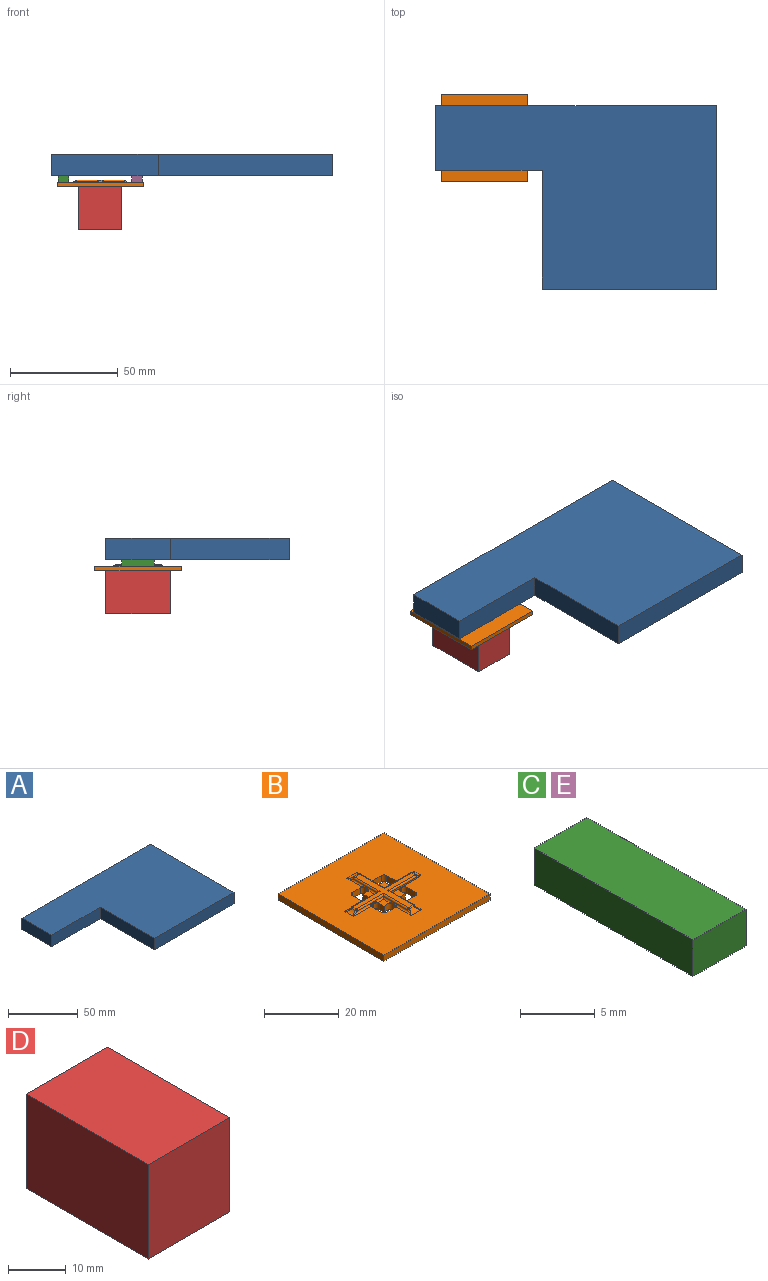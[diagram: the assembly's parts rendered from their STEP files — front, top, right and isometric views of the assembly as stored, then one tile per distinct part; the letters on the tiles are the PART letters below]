
ASSEMBLY  parts=5 mates=4
PART A: 8 faces, bbox 130x84.9x10 mm
  f0: plane 49.29x10mm, normal (0,-1,0), area 492.9mm2, adj f1,f5,f6,f7
  f1: plane 54.94x10mm, normal (-1,0,0), area 549.4mm2, adj f0,f2,f6,f7
  f2: plane 80.71x10mm, normal (0,-1,0), area 807.1mm2, adj f1,f3,f6,f7
  f3: plane 84.94x10mm, normal (1,0,0), area 849.4mm2, adj f2,f4,f6,f7
  f4: plane 130x10mm, normal (0,1,0), area 1300mm2, adj f3,f5,f6,f7
  f5: plane 30x10mm, normal (-1,0,0), area 300mm2, adj f0,f4,f6,f7
  f6: plane 130x84.94mm, normal (0,0,1), area 8334mm2, adj f0,f1,f2,f3,f4,f5
  f7: plane 130x84.94mm, normal (0,0,-1), area 8334mm2, adj f0,f1,f2,f3,f4,f5
PART B: 123 faces, bbox 40.1x40.1x3.1 mm
  f0: plane 40.13x40.13mm, normal (0,0,1), area 1357.2mm2, adj f3,f4,f5,f10,f11,f12,f13,f14
  f1: plane 2.59x2.31mm, normal (0,0,1), area 5.1mm2, adj f7,f8,f39,f40,f76,f79
  f2: plane 2.59x2.31mm, normal (0,0,1), area 5.1mm2, adj f22,f23,f36,f42,f95,f98
  f3: plane 40x2mm, normal (1,0,0), area 80mm2, adj f0,f4,f30,f32
  f4: plane 40x2mm, normal (0,1,0), area 80mm2, adj f0,f3,f5,f32
  f5: plane 40x2mm, normal (-1,0,0), area 80mm2, adj f0,f4,f30,f32
  f6: plane 2x0.5mm, normal (0,1,0), area 1mm2, adj f32,f39,f49,f80
  f7: plane 2x1.79mm, normal (1,0,0), area 3.6mm2, adj f1,f8,f32,f39
  f8: plane 2x1.5mm, normal (0,1,0), area 3mm2, adj f1,f7,f32,f40
  f9: plane 2x0.5mm, normal (1,0,0), area 1mm2, adj f32,f40,f47,f72
  f10: plane 3x2mm, normal (0,-1,0), area 6mm2, adj f0,f32,f47,f48
  f11: plane 2x1.79mm, normal (1,0,0), area 3.6mm2, adj f0,f27,f32,f38
  f12: plane 2x0.5mm, normal (0,-1,0), area 1mm2, adj f0,f32,f38,f50
  f13: plane 3.29x2mm, normal (-1,0,0), area 6.6mm2, adj f0,f32,f50,f51
  f14: plane 4x2.19mm, normal (0,1,0), area 8mm2, adj f0,f15,f32,f51,f86
  f15: plane 2.19x1.5mm, normal (1,0,0), area 3.3mm2, adj f14,f32,f37,f86
  f16: plane 2x1.79mm, normal (-1,0,0), area 3.6mm2, adj f28,f31,f32,f33
  f17: plane 2x0.5mm, normal (0,1,0), area 1mm2, adj f32,f33,f34,f67
  f18: plane 3.29x2mm, normal (1,0,0), area 6.6mm2, adj f0,f32,f34,f45
  f19: plane 3x2mm, normal (0,-1,0), area 6mm2, adj f0,f32,f45,f46
  f20: plane 2x0.5mm, normal (-1,0,0), area 1mm2, adj f32,f41,f46,f61
  f21: plane 2x0.5mm, normal (0,-1,0), area 1mm2, adj f32,f35,f36,f88
  f22: plane 2x1.79mm, normal (-1,0,0), area 3.6mm2, adj f2,f23,f32,f36
  f23: plane 2x1.5mm, normal (0,-1,0), area 3mm2, adj f2,f22,f32,f42
  f24: plane 2x0.5mm, normal (-1,0,0), area 1mm2, adj f32,f42,f43,f94
  f25: plane 3x2mm, normal (0,1,0), area 6mm2, adj f0,f32,f43,f44
  f26: plane 3.29x2mm, normal (-1,0,0), area 6.6mm2, adj f0,f32,f48,f49
  f27: plane 2x1.5mm, normal (0,-1,0), area 3mm2, adj f0,f11,f32,f37
  f28: plane 2x1.5mm, normal (0,1,0), area 3mm2, adj f16,f31,f32,f41
  f29: plane 3.29x2mm, normal (1,0,0), area 6.6mm2, adj f0,f32,f35,f44
  f30: plane 40x2mm, normal (0,-1,0), area 80mm2, adj f0,f3,f5,f32
  f31: plane 2.59x2.31mm, normal (0,0,1), area 5.1mm2, adj f16,f28,f33,f41,f68,f71
  f32: plane 40x40mm, normal (0,0,-1), area 1526.2mm2, adj f3,f4,f5,f6,f7,f8,f9,f10
  f33: cylinder r=1mm len=2mm, axis (0,0,1), area 3.1mm2, adj f16,f17,f31,f32,f70
  f34: cylinder r=1mm len=2mm, axis (0,0,-1), area 3.1mm2, adj f0,f17,f18,f32,f63
  f35: cylinder r=1mm len=2mm, axis (0,0,1), area 3.1mm2, adj f0,f21,f29,f32,f87
  f36: cylinder r=1mm len=2mm, axis (0,0,-1), area 3.1mm2, adj f2,f21,f22,f32,f91
  f37: cylinder r=1mm len=2.19mm, axis (0,0,-1), area 3.2mm2, adj f0,f15,f27,f32,f86
  f38: cylinder r=1mm len=2mm, axis (0,0,1), area 3.1mm2, adj f0,f11,f12,f32
  f39: cylinder r=1mm len=2mm, axis (0,0,-1), area 3.1mm2, adj f1,f6,f7,f32,f77
  f40: cylinder r=1mm len=2mm, axis (0,0,1), area 3.1mm2, adj f1,f8,f9,f32,f74
  f41: cylinder r=1mm len=2mm, axis (0,0,-1), area 3.1mm2, adj f20,f28,f31,f32,f64
  f42: cylinder r=1mm len=2mm, axis (0,0,1), area 3.1mm2, adj f2,f23,f24,f32,f97
  f43: cylinder r=1mm len=2mm, axis (0,0,-1), area 3.1mm2, adj f0,f24,f25,f32,f90
  f44: cylinder r=1mm len=2mm, axis (0,0,-1), area 3.1mm2, adj f0,f25,f29,f32
  f45: cylinder r=1mm len=2mm, axis (0,0,1), area 3.1mm2, adj f0,f18,f19,f32
  f46: cylinder r=1mm len=2mm, axis (0,0,1), area 3.1mm2, adj f0,f19,f20,f32,f60
  f47: cylinder r=1mm len=2mm, axis (0,0,-1), area 3.1mm2, adj f0,f9,f10,f32,f73
  f48: cylinder r=1mm len=2mm, axis (0,0,-1), area 3.1mm2, adj f0,f10,f26,f32
  f49: cylinder r=1mm len=2mm, axis (0,0,1), area 3.1mm2, adj f0,f6,f26,f32,f82
  f50: cylinder r=1mm len=2mm, axis (0,0,-1), area 3.1mm2, adj f0,f12,f13,f32
  f51: cylinder r=1mm len=2mm, axis (0,0,1), area 3.1mm2, adj f0,f13,f14,f32
  f52: plane 2.11x0.2mm, normal (0,-1,0), area 0.3mm2, adj f87,f88,f91,f92
  f53: plane 2.08x0.19mm, normal (-1,0,0), area 0.2mm2, adj f90,f94,f96,f97
  f54: plane 10.25x0.5mm, normal (0,-1,0), area 4.9mm2, adj f0,f84,f86,f113
  f55: plane 2.11x0.2mm, normal (0,1,0), area 0.3mm2, adj f77,f80,f81,f82
  f56: plane 2.09x0.19mm, normal (1,0,0), area 0.2mm2, adj f72,f73,f74,f78
  f57: plane 2.08x0.19mm, normal (-1,0,0), area 0.2mm2, adj f60,f61,f64,f65
  f58: plane 2.11x0.2mm, normal (0,1,0), area 0.3mm2, adj f63,f67,f69,f70
  f59: plane 22.28x20.2mm, normal (0,0,1), area 61.2mm2, adj f65,f69,f78,f81,f84,f85,f92,f96
  f60: bspline ~0.98x0.52mm, area 0.4mm2, adj f46,f57,f61,f62
  f61: cylinder r=0.5mm len=0.5mm, axis (0,-1,0), area 0.2mm2, adj f20,f57,f60,f64
  f62: cylinder r=0.5mm len=5.81mm, axis (0,-1,0), area 3.7mm2, adj f0,f60,f65,f108
  f63: bspline ~1x0.54mm, area 0.4mm2, adj f34,f58,f66,f67
  f64: bspline ~1x0.57mm, area 0.4mm2, adj f41,f57,f61,f68
  f65: cylinder r=0.5mm len=9.48mm, axis (0,1,0), area 7.2mm2, adj f57,f59,f62,f68,f69,f109
  f66: cylinder r=0.5mm len=6.84mm, axis (-1,0,0), area 4.5mm2, adj f0,f63,f69,f107
  f67: cylinder r=0.5mm len=0.5mm, axis (1,0,0), area 0.2mm2, adj f17,f58,f63,f70
  f68: cylinder r=0.5mm len=3.09mm, axis (0,-1,0), area 2.3mm2, adj f31,f64,f65,f71
  f69: cylinder r=0.5mm len=10.25mm, axis (1,0,0), area 7.8mm2, adj f58,f59,f65,f66,f71,f106
  f70: bspline ~0.96x0.52mm, area 0.4mm2, adj f33,f58,f67,f71
  f71: cylinder r=0.5mm len=2.81mm, axis (-1,0,0), area 2.1mm2, adj f31,f68,f69,f70
  f72: cylinder r=0.5mm len=0.5mm, axis (0,-1,0), area 0.2mm2, adj f9,f56,f73,f74
  f73: bspline ~1x0.57mm, area 0.4mm2, adj f47,f56,f72,f75
  f74: bspline ~0.98x0.52mm, area 0.4mm2, adj f40,f56,f72,f76
  f75: cylinder r=0.5mm len=5.81mm, axis (0,1,0), area 3.7mm2, adj f0,f73,f78,f112
  f76: cylinder r=0.5mm len=3.09mm, axis (0,1,0), area 2.3mm2, adj f1,f74,f78,f79
  f77: bspline ~1x0.54mm, area 0.4mm2, adj f39,f55,f79,f80
  f78: cylinder r=0.5mm len=9.48mm, axis (0,-1,0), area 7.2mm2, adj f56,f59,f75,f76,f81,f111
  f79: cylinder r=0.5mm len=2.81mm, axis (-1,0,0), area 2.1mm2, adj f1,f76,f77,f81
  f80: cylinder r=0.5mm len=0.5mm, axis (1,0,0), area 0.2mm2, adj f6,f55,f77,f82
  f81: cylinder r=0.5mm len=10.25mm, axis (1,0,0), area 7.8mm2, adj f55,f59,f78,f79,f83,f116
  f82: bspline ~0.96x0.52mm, area 0.4mm2, adj f49,f55,f80,f83
  f83: cylinder r=0.5mm len=6.84mm, axis (-1,0,0), area 4.5mm2, adj f0,f81,f82,f117
  f84: cylinder r=0.5mm len=10.25mm, axis (-1,0,0), area 7.8mm2, adj f54,f59,f85,f114
  f85: cylinder r=0.5mm len=9.48mm, axis (0,-1,0), area 7.2mm2, adj f59,f84,f86,f121
  f86: cylinder r=0.5mm len=10.98mm, axis (0,1,0), area 6.8mm2, adj f0,f14,f15,f37,f54,f85,f122
  f87: bspline ~0.96x0.52mm, area 0.4mm2, adj f35,f52,f88,f89
  f88: cylinder r=0.5mm len=0.5mm, axis (1,0,0), area 0.2mm2, adj f21,f52,f87,f91
  f89: cylinder r=0.5mm len=6.84mm, axis (1,0,0), area 4.5mm2, adj f0,f87,f92,f103
  f90: bspline ~1x0.57mm, area 0.4mm2, adj f43,f53,f93,f94
  f91: bspline ~1x0.54mm, area 0.4mm2, adj f36,f52,f88,f95
  f92: cylinder r=0.5mm len=10.25mm, axis (-1,0,0), area 7.8mm2, adj f52,f59,f89,f95,f96,f104
  f93: cylinder r=0.5mm len=5.81mm, axis (0,-1,0), area 3.7mm2, adj f0,f90,f96,f118
  f94: cylinder r=0.5mm len=0.5mm, axis (0,-1,0), area 0.2mm2, adj f24,f53,f90,f97
  f95: cylinder r=0.5mm len=2.81mm, axis (1,0,0), area 2.1mm2, adj f2,f91,f92,f98
  f96: cylinder r=0.5mm len=9.48mm, axis (0,1,0), area 7.2mm2, adj f53,f59,f92,f93,f98,f119
  f97: bspline ~0.98x0.52mm, area 0.4mm2, adj f42,f53,f94,f98
  f98: cylinder r=0.5mm len=3.09mm, axis (0,-1,0), area 2.3mm2, adj f2,f95,f96,f97
  f99: cylinder r=2mm len=3.24mm, axis (0,-1,0), area 3.7mm2, adj f0,f103,f105,f107
  f100: cylinder r=2mm len=2.24mm, axis (0,-1,0), area 3mm2, adj f0,f113,f115,f117
  f101: cylinder r=2mm len=3.78mm, axis (-1,0,0), area 4.7mm2, adj f0,f108,f110,f112
  f102: cylinder r=2mm len=3.78mm, axis (-1,0,0), area 4.7mm2, adj f0,f118,f120,f122
  f103: bspline ~2x1mm, area 0.8mm2, adj f89,f99,f104
  f104: sphere r=0.5mm, area 0.2mm2, adj f92,f103,f105
  f105: cylinder r=0.5mm len=1.24mm, axis (0,-1,0), area 0.6mm2, adj f59,f99,f104,f106
  f106: sphere r=0.5mm, area 0.2mm2, adj f69,f105,f107
  f107: bspline ~2x1mm, area 0.8mm2, adj f66,f99,f106
  f108: bspline ~2.14x1mm, area 0.7mm2, adj f62,f101,f109
  f109: sphere r=0.5mm, area 0.2mm2, adj f65,f108,f110
  f110: cylinder r=0.5mm len=1.78mm, axis (-1,0,0), area 0.8mm2, adj f59,f101,f109,f111
  f111: sphere r=0.5mm, area 0.2mm2, adj f78,f110,f112
  f112: bspline ~2.14x1mm, area 0.7mm2, adj f75,f101,f111
  f113: torus R=2.5mm, axis (0,-1,0), area 1mm2, adj f0,f54,f100,f114
  f114: sphere r=0.5mm, area 0.2mm2, adj f84,f113,f115
  f115: cylinder r=0.5mm len=1.24mm, axis (0,-1,0), area 0.6mm2, adj f59,f100,f114,f116
  f116: sphere r=0.5mm, area 0.2mm2, adj f81,f115,f117
  f117: bspline ~2x1mm, area 0.8mm2, adj f83,f100,f116
  f118: bspline ~2.14x1mm, area 0.7mm2, adj f93,f102,f119
  f119: sphere r=0.5mm, area 0.2mm2, adj f96,f118,f120
  f120: cylinder r=0.5mm len=1.78mm, axis (-1,0,0), area 0.8mm2, adj f59,f102,f119,f121
  f121: sphere r=0.5mm, area 0.2mm2, adj f85,f120,f122
  f122: bspline ~2.14x1mm, area 0.7mm2, adj f86,f102,f121
PART C: 6 faces, bbox 5x15x3 mm
  f0: plane 15x3mm, normal (1,0,0), area 45mm2, adj f1,f3,f4,f5
  f1: plane 5x3mm, normal (0,1,0), area 15mm2, adj f0,f2,f4,f5
  f2: plane 15x3mm, normal (-1,0,0), area 45mm2, adj f1,f3,f4,f5
  f3: plane 5x3mm, normal (0,-1,0), area 15mm2, adj f0,f2,f4,f5
  f4: plane 15x5mm, normal (0,0,1), area 75mm2, adj f0,f1,f2,f3
  f5: plane 15x5mm, normal (0,0,-1), area 75mm2, adj f0,f1,f2,f3
PART D: 6 faces, bbox 20x30x20 mm
  f0: plane 30x20mm, normal (-1,0,0), area 600mm2, adj f1,f3,f4,f5
  f1: plane 20x20mm, normal (0,-1,0), area 400mm2, adj f0,f2,f4,f5
  f2: plane 30x20mm, normal (1,0,0), area 600mm2, adj f1,f3,f4,f5
  f3: plane 20x20mm, normal (0,1,0), area 400mm2, adj f0,f2,f4,f5
  f4: plane 30x20mm, normal (0,0,1), area 600mm2, adj f0,f1,f2,f3
  f5: plane 30x20mm, normal (0,0,-1), area 600mm2, adj f0,f1,f2,f3
PART E: same geometry as C
PLACE A t=(-11.05,-31.24,-25.43)mm
PLACE B t=(11.45,-16.24,-30.43)mm
PLACE C rot(axis=(1,0,0),180deg) t=(-5.55,-16.24,-25.43)mm
PLACE D t=(1.45,-31.23,-50.43)mm
PLACE E t=(28.45,-16.24,-28.43)mm
MATE fastened E.f5 <-> B.f0  axis (0,0,-1) through (28.45,-16.24,-28.43)mm
MATE fastened C.f4 <-> B.f0  axis (0,0,-1) through (-5.55,-16.24,-28.43)mm
MATE fastened D.f4 <-> B.f32  axis (0,0,1) through (11.45,-16.23,-30.43)mm
MATE fastened A.f7 <-> C.f5  axis (0,0,-1) through (-8.05,-16.24,-25.43)mm
